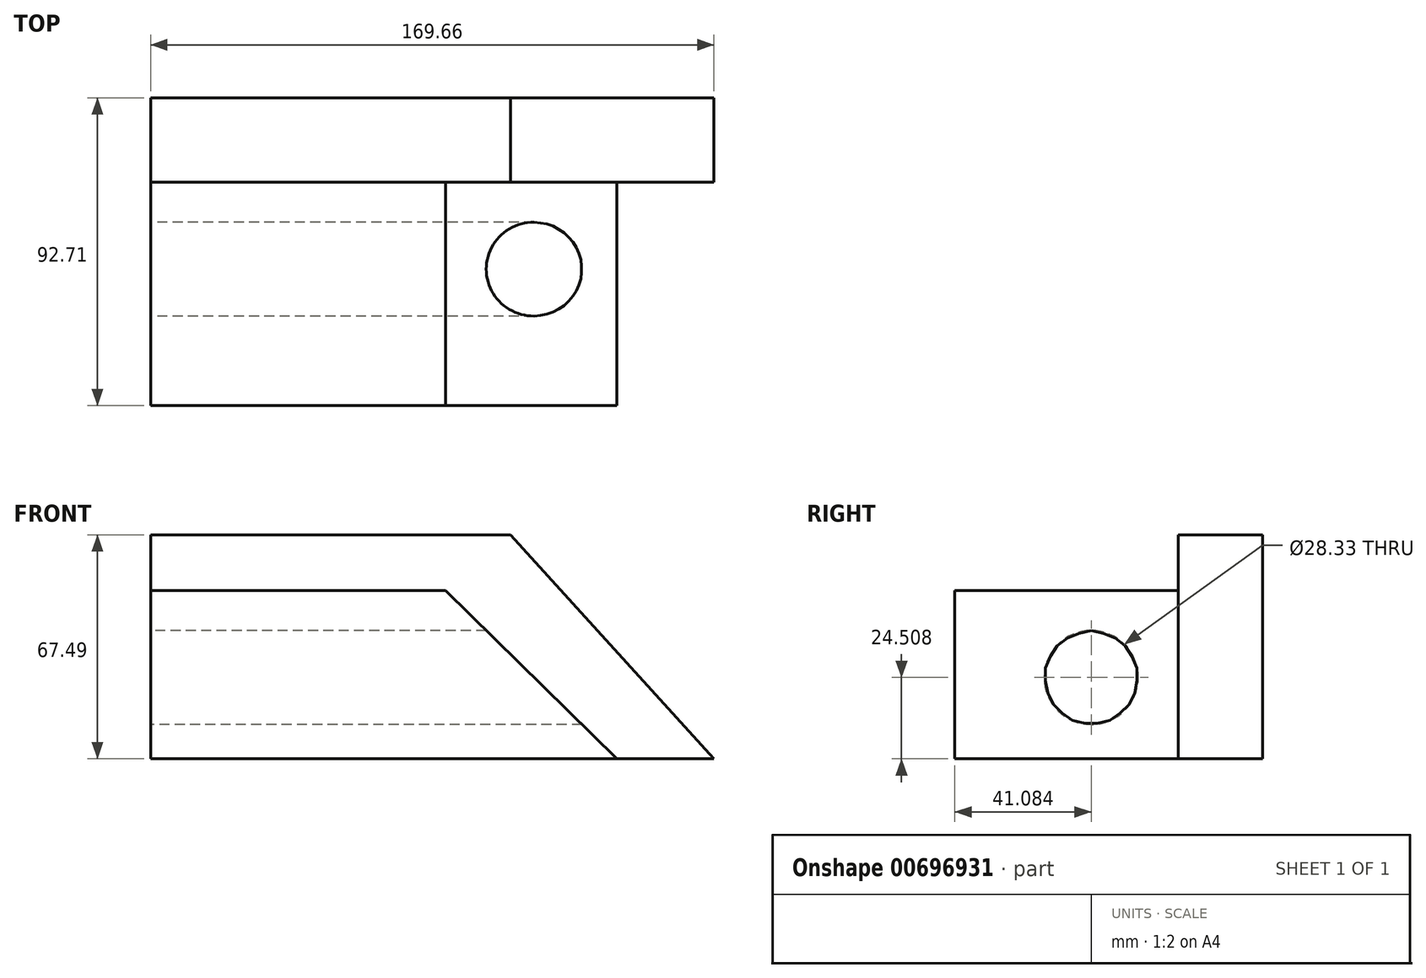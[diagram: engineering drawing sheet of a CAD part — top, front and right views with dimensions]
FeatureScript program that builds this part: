
annotation { "Feature Type Name" : "Feature", "Feature Type Description" : "" }
export const myFeature = defineFeature(function(context is Context, id is Id, definition is map)
    precondition{}
    {
        {
            var Q0;
            Q0=qCreatedBy(makeId("Front.planeOp"),FACE);
            var sketch = newSketch(context, id + "F0", { "sketchPlane" : qUnion([Q0])});
            skLineSegment(sketch, "E0", {"start": v(0, 0) * mm, "end": v(0, 50.7) * mm});
            skLineSegment(sketch, "E1", {"start": v(0, 50.7) * mm, "end": v(88.8, 50.7) * mm});
            skLineSegment(sketch, "E2", {"start": v(88.8, 50.7) * mm, "end": v(140.42, 0) * mm});
            skLineSegment(sketch, "E3", {"start": v(140.42, 0) * mm, "end": v(0, 0) * mm});
            skLineSegment(sketch, "E4", {"start": v(0, 0) * mm, "end": v(0, 67.49) * mm});
            skLineSegment(sketch, "E5", {"start": v(0, 67.49) * mm, "end": v(108.39, 67.49) * mm});
            skLineSegment(sketch, "E6", {"start": v(108.39, 67.49) * mm, "end": v(169.66, 0) * mm});
            skLineSegment(sketch, "E7", {"start": v(169.66, 0) * mm, "end": v(140.42, 0) * mm});
            skSolve(sketch);
        }
        {
            var Q0;
            {var subQ0=sQuery(id+"F0.wireOp",EDGE,"E1");Q0=makeQuery(id+"F0.imprint","IMPRINT",FACE,{"disambiguationData":[TD([[makeQuery(id+"F0.imprint","IMPRINT",EDGE,{"derivedFrom":subQ0}),-1.0]])]});}
            extrude(context, id + "F1", {"entities" : qUnion([Q0]), "depth" : 92.7 * mm, "offsetDistance" : 25.4 * mm});
        }
        {
            var Q0;
            {var subQ1=sQuery(id+"F0.wireOp",EDGE,"E1");Q0=makeQuery(id+"F0.imprint","IMPRINT",FACE,{"disambiguationData":[TD([[makeQuery(id+"F0.imprint","IMPRINT",EDGE,{"derivedFrom":subQ1}),1.0]])]});}
            extrude(context, id + "F2", {"entities" : qUnion([Q0]), "operationType" : NewBodyOperationType.ADD, "depth" : 25.4 * mm, "offsetDistance" : 25.4 * mm});
        }
        {
            var Q0;
            {var subQ0=sQuery(id+"F0.wireOp",EDGE,"E4");Q0=makeQuery(id+"F2.boolean.opBoolean","MERGE",FACE,{"derivedFrom":[makeQuery(id+"F1.opExtrude","SWEPT_FACE",FACE,{"disambiguationData":[OSD([subQ0])]}),makeQuery(id+"F2.opExtrude","SWEPT_FACE",FACE,{"disambiguationData":[OSD([subQ0])]})]});}
            var sketch = newSketch(context, id + "F3", { "sketchPlane" : qUnion([Q0])});
            skCircle(sketch, "E8", {"center": v(51.63, 24.5) * mm, "radius": 14.16 * mm});
            skSolve(sketch);
        }
        {
            var Q0;
            Q0 = qSketchRegion(id + "F3", true);
            extrude(context, id + "F4", {"entities" : qUnion([Q0]), "operationType" : NewBodyOperationType.REMOVE, "oppositeDirection" : true, "depth" : 161.54 * mm, "offsetDistance" : 25.4 * mm});
        }
    });
